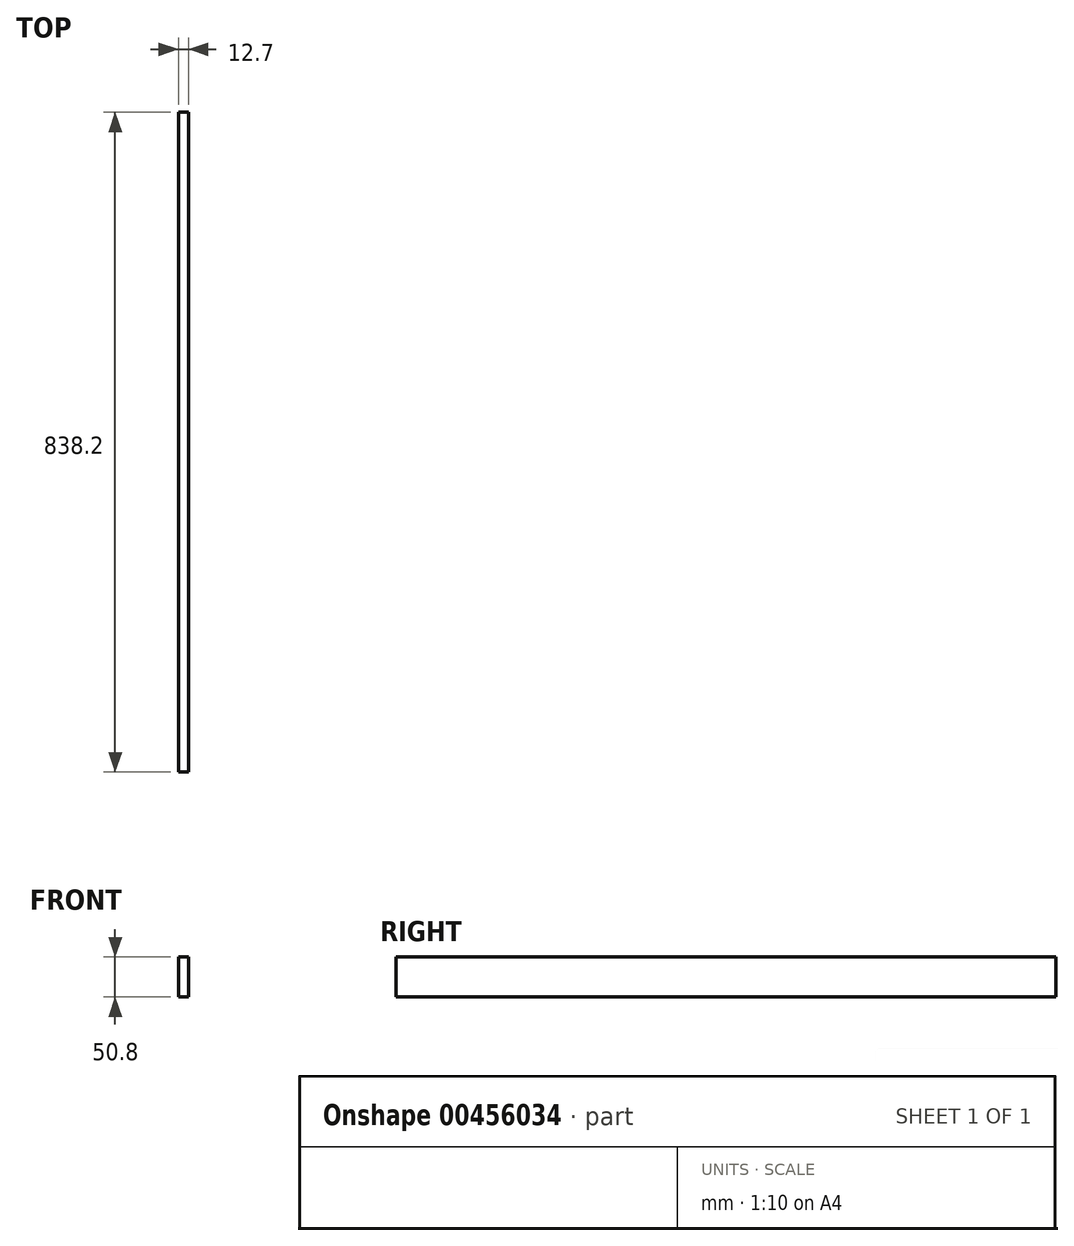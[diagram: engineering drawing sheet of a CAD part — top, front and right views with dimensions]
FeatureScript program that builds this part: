
annotation { "Feature Type Name" : "Feature", "Feature Type Description" : "" }
export const myFeature = defineFeature(function(context is Context, id is Id, definition is map)
    precondition{}
    {
        {
            var Q0;
            Q0=qCreatedBy(makeId("Top.planeOp"),FACE);
            var sketch = newSketch(context, id + "F0", { "sketchPlane" : qUnion([Q0])});
            skLineSegment(sketch, "E0.bottom", {"start": v(0, 0) * mm, "end": v(-12.7, 0) * mm});
            skLineSegment(sketch, "E0.top", {"start": v(0, -838.2) * mm, "end": v(-12.7, -838.2) * mm});
            skLineSegment(sketch, "E0.left", {"start": v(0, 0) * mm, "end": v(0, -838.2) * mm});
            skLineSegment(sketch, "E0.right", {"start": v(-12.7, 0) * mm, "end": v(-12.7, -838.2) * mm});
            skSolve(sketch);
        }
        {
            var Q0;
            Q0=makeQuery(id+"F0.imprint","IMPRINT",FACE,{"disambiguationData":[TD([[makeQuery(id+"F0.imprint","IMPRINT",EDGE,{"derivedFrom":sQuery(id+"F0.wireOp",EDGE,"E0.bottom")}),1.0]])]});
            extrude(context, id + "F1", {"entities" : qUnion([Q0]), "depth" : 50.8 * mm});
        }
    });
